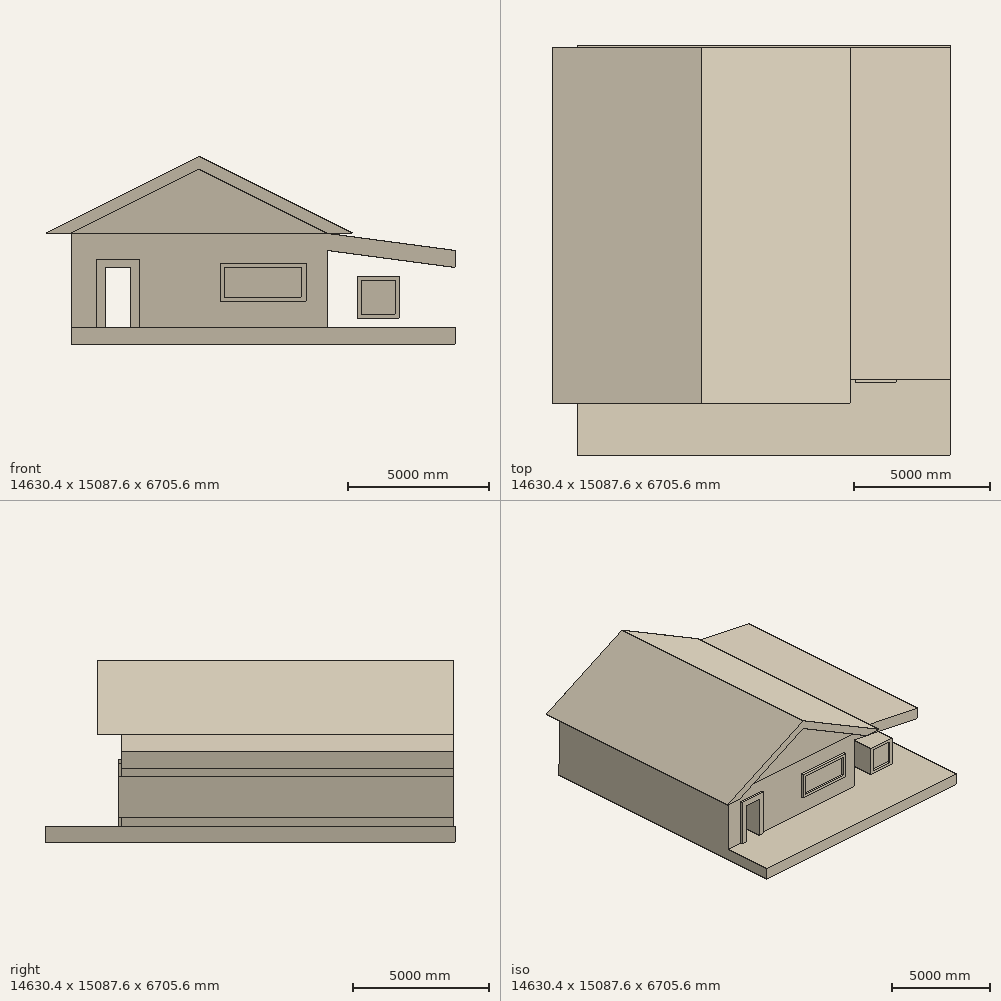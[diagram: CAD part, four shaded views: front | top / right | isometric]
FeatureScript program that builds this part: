
annotation { "Feature Type Name" : "Feature", "Feature Type Description" : "" }
export const myFeature = defineFeature(function(context is Context, id is Id, definition is map)
    precondition{}
    {
        {
            var Q0;
            Q0=qCreatedBy(makeId("Front.planeOp"),FACE);
            var sketch = newSketch(context, id + "F0", { "sketchPlane" : qUnion([Q0])});
            skLineSegment(sketch, "E0.bottom", {"start": v(-4572, 1676.4) * mm, "end": v(4572, 1676.4) * mm});
            skLineSegment(sketch, "E0.top", {"start": v(-4572, -1676.4) * mm, "end": v(4572, -1676.4) * mm});
            skLineSegment(sketch, "E0.left", {"start": v(-4572, 1676.4) * mm, "end": v(-4572, -1676.4) * mm});
            skLineSegment(sketch, "E0.right", {"start": v(4572, 1676.4) * mm, "end": v(4572, -1676.4) * mm});
            skPoint(sketch, "E0.middle", {"position": v(0, 0) * mm});
            skLineSegment(sketch, "E1", {"start": v(0, 1676.4) * mm, "end": v(0, 3962.4) * mm});
            skPoint(sketch, "E1.endSnap0", {"position": v(0, 1676.4) * mm});
            skLineSegment(sketch, "E2", {"start": v(0, 3962.4) * mm, "end": v(-4572, 1676.4) * mm});
            skLineSegment(sketch, "E3", {"start": v(0, 3962.4) * mm, "end": v(4572, 1676.4) * mm});
            skLineSegment(sketch, "E4", {"start": v(0, 3962.4) * mm, "end": v(0, 4419.6) * mm});
            skLineSegment(sketch, "E5", {"start": v(-4572, 1676.4) * mm, "end": v(-5486.4, 1676.4) * mm});
            skLineSegment(sketch, "E6", {"start": v(4572, 1676.4) * mm, "end": v(5486.4, 1676.4) * mm});
            skLineSegment(sketch, "E7", {"start": v(-5486.4, 1676.4) * mm, "end": v(0, 4419.6) * mm});
            skLineSegment(sketch, "E8", {"start": v(5486.4, 1676.4) * mm, "end": v(0, 4419.6) * mm});
            skLineSegment(sketch, "E9", {"start": v(-4572, -1676.4) * mm, "end": v(-4572, -2286) * mm});
            skLineSegment(sketch, "E10", {"start": v(4572, -1676.4) * mm, "end": v(4572, -2286) * mm});
            skLineSegment(sketch, "E11", {"start": v(4572, -2286) * mm, "end": v(-4572, -2286) * mm});
            skLineSegment(sketch, "E12", {"start": v(4572, -2286) * mm, "end": v(9144, -2286) * mm});
            skLineSegment(sketch, "E13", {"start": v(9144, -2286) * mm, "end": v(9144, -1676.4) * mm});
            skLineSegment(sketch, "E14", {"start": v(9144, -1676.4) * mm, "end": v(4572, -1676.4) * mm});
            skLineSegment(sketch, "E15", {"start": v(9144, -1676.4) * mm, "end": v(9144, 1066.8) * mm});
            skLineSegment(sketch, "E16", {"start": v(9144, 1066.8) * mm, "end": v(9144, 457.2) * mm});
            skLineSegment(sketch, "E17", {"start": v(4572, 1676.4) * mm, "end": v(4572, 1066.8) * mm});
            skLineSegment(sketch, "E18", {"start": v(9144, 457.2) * mm, "end": v(4572, 1066.8) * mm});
            skLineSegment(sketch, "E19", {"start": v(9144, 1066.8) * mm, "end": v(4572, 1676.4) * mm});
            skLineSegment(sketch, "E20.bottom", {"start": v(914.4, 457.2) * mm, "end": v(3657.6, 457.2) * mm});
            skLineSegment(sketch, "E20.top", {"start": v(914.4, -609.6) * mm, "end": v(3657.6, -609.6) * mm});
            skLineSegment(sketch, "E20.left", {"start": v(914.4, 457.2) * mm, "end": v(914.4, -609.6) * mm});
            skLineSegment(sketch, "E20.right", {"start": v(3657.6, 457.2) * mm, "end": v(3657.6, -609.6) * mm});
            skLineSegment(sketch, "E21.0", {"start": v(762, 609.6) * mm, "end": v(3810, 609.6) * mm});
            skLineSegment(sketch, "E21.1", {"start": v(762, 609.6) * mm, "end": v(762, -762) * mm});
            skLineSegment(sketch, "E21.2", {"start": v(762, -762) * mm, "end": v(3810, -762) * mm});
            skLineSegment(sketch, "E21.3", {"start": v(3810, 609.6) * mm, "end": v(3810, -762) * mm});
            skLineSegment(sketch, "E22.bottom", {"start": v(5791.2, 0) * mm, "end": v(7010.4, 0) * mm});
            skLineSegment(sketch, "E22.top", {"start": v(5791.2, -1219.2) * mm, "end": v(7010.4, -1219.2) * mm});
            skLineSegment(sketch, "E22.left", {"start": v(5791.2, 0) * mm, "end": v(5791.2, -1219.2) * mm});
            skLineSegment(sketch, "E22.right", {"start": v(7010.4, 0) * mm, "end": v(7010.4, -1219.2) * mm});
            skLineSegment(sketch, "E23.0", {"start": v(5638.8, 152.4) * mm, "end": v(7162.8, 152.4) * mm});
            skLineSegment(sketch, "E23.1", {"start": v(5638.8, 152.4) * mm, "end": v(5638.8, -1371.6) * mm});
            skLineSegment(sketch, "E23.2", {"start": v(5638.8, -1371.6) * mm, "end": v(7162.8, -1371.6) * mm});
            skLineSegment(sketch, "E23.3", {"start": v(7162.8, 152.4) * mm, "end": v(7162.8, -1371.6) * mm});
            skLineSegment(sketch, "E24.bottom", {"start": v(-3352.8, -1676.4) * mm, "end": v(-2438.4, -1676.4) * mm});
            skLineSegment(sketch, "E24.top", {"start": v(-3352.8, 457.2) * mm, "end": v(-2438.4, 457.2) * mm});
            skLineSegment(sketch, "E24.left", {"start": v(-3352.8, -1676.4) * mm, "end": v(-3352.8, 457.2) * mm});
            skLineSegment(sketch, "E24.right", {"start": v(-2438.4, -1676.4) * mm, "end": v(-2438.4, 457.2) * mm});
            skLineSegment(sketch, "E25.0", {"start": v(-2133.6, -1676.4) * mm, "end": v(-2133.6, 762) * mm});
            skLineSegment(sketch, "E25.1", {"start": v(-3657.6, 762) * mm, "end": v(-2133.6, 762) * mm});
            skLineSegment(sketch, "E25.2", {"start": v(-3657.6, -1676.4) * mm, "end": v(-3657.6, 762) * mm});
            skSolve(sketch);
        }
        {
            var Q0;
            Q0=makeQuery(id+"F0.imprint","IMPRINT",FACE,{"disambiguationData":[TD([[makeQuery(id+"F0.imprint","IMPRINT",EDGE,{"derivedFrom":sQuery(id+"F0.wireOp",EDGE,"E2")}),-1.0]])]});
            var Q1;
            Q1=makeQuery(id+"F0.imprint","IMPRINT",FACE,{"disambiguationData":[TD([[makeQuery(id+"F0.imprint","IMPRINT",EDGE,{"derivedFrom":sQuery(id+"F0.wireOp",EDGE,"E3")}),1.0]])]});
            var Q2;
            Q2=makeQuery(id+"F0.imprint","IMPRINT",FACE,{"disambiguationData":[TD([[makeQuery(id+"F0.imprint","IMPRINT",EDGE,{"derivedFrom":sQuery(id+"F0.wireOp",EDGE,"E16")}),-1.0]])]});
            extrude(context, id + "F1", {"entities" : qUnion([Q0, Q1, Q2]), "depth" : 914.4 * mm, "offsetDistance" : 30.48 * mm, "hasSecondDirection" : true, "secondDirectionOppositeDirection" : true, "secondDirectionDepth" : 12192 * mm});
        }
        {
            var Q0;
            {var subQ2=sQuery(id+"F0.wireOp",EDGE,"E1");Q0=makeQuery(id+"F0.imprint","IMPRINT",FACE,{"disambiguationData":[TD([[makeQuery(id+"F0.imprint","IMPRINT",EDGE,{"derivedFrom":subQ2}),1.0]])]});}
            var Q1;
            {var subQ2=sQuery(id+"F0.wireOp",EDGE,"E1");Q1=makeQuery(id+"F0.imprint","IMPRINT",FACE,{"disambiguationData":[TD([[makeQuery(id+"F0.imprint","IMPRINT",EDGE,{"derivedFrom":subQ2}),-1.0]])]});}
            extrude(context, id + "F2", {"entities" : qUnion([Q0, Q1]), "operationType" : NewBodyOperationType.ADD, "depth" : 304.8 * mm, "offsetDistance" : 30.48 * mm, "hasSecondDirection" : true, "secondDirectionOppositeDirection" : true, "secondDirectionDepth" : 12192 * mm});
        }
        {
            var Q0;
            {var subQ1=sQuery(id+"F0.wireOp",EDGE,"E0.left");Q0=makeQuery(id+"F0.imprint","IMPRINT",FACE,{"disambiguationData":[TD([[makeQuery(id+"F0.imprint","IMPRINT",EDGE,{"derivedFrom":subQ1}),1.0]])]});}
            var Q1;
            Q1=makeQuery(id+"F0.imprint","IMPRINT",FACE,{"disambiguationData":[TD([[makeQuery(id+"F0.imprint","IMPRINT",EDGE,{"derivedFrom":sQuery(id+"F0.wireOp",EDGE,"E24.bottom")}),1.0]])]});
            var Q2;
            Q2=makeQuery(id+"F0.imprint","IMPRINT",FACE,{"disambiguationData":[TD([[makeQuery(id+"F0.imprint","IMPRINT",EDGE,{"derivedFrom":sQuery(id+"F0.wireOp",EDGE,"E24.top")}),1.0]])]});
            var Q3;
            Q3=makeQuery(id+"F0.imprint","IMPRINT",FACE,{"disambiguationData":[TD([[makeQuery(id+"F0.imprint","IMPRINT",EDGE,{"derivedFrom":sQuery(id+"F0.wireOp",EDGE,"E20.bottom")}),-1.0]])]});
            var Q4;
            Q4=makeQuery(id+"F0.imprint","IMPRINT",FACE,{"disambiguationData":[TD([[makeQuery(id+"F0.imprint","IMPRINT",EDGE,{"derivedFrom":sQuery(id+"F0.wireOp",EDGE,"E20.bottom")}),1.0]])]});
            var Q5;
            Q5=makeQuery(id+"F0.imprint","IMPRINT",FACE,{"disambiguationData":[TD([[makeQuery(id+"F0.imprint","IMPRINT",EDGE,{"derivedFrom":sQuery(id+"F0.wireOp",EDGE,"E0.right")}),1.0]])]});
            var Q6;
            Q6=makeQuery(id+"F0.imprint","IMPRINT",FACE,{"disambiguationData":[TD([[makeQuery(id+"F0.imprint","IMPRINT",EDGE,{"derivedFrom":sQuery(id+"F0.wireOp",EDGE,"E22.bottom")}),-1.0]])]});
            var Q7;
            Q7=makeQuery(id+"F0.imprint","IMPRINT",FACE,{"disambiguationData":[TD([[makeQuery(id+"F0.imprint","IMPRINT",EDGE,{"derivedFrom":sQuery(id+"F0.wireOp",EDGE,"E22.bottom")}),1.0]])]});
            extrude(context, id + "F3", {"entities" : qUnion([Q0, Q1, Q2, Q3, Q4, Q5, Q6, Q7]), "depth" : 30.48 * mm, "offsetDistance" : 30.48 * mm, "hasSecondDirection" : true, "secondDirectionOppositeDirection" : true, "secondDirectionDepth" : 12192 * mm});
        }
        {
            var Q0;
            Q0=makeQuery(id+"F0.imprint","IMPRINT",FACE,{"disambiguationData":[TD([[makeQuery(id+"F0.imprint","IMPRINT",EDGE,{"derivedFrom":sQuery(id+"F0.wireOp",EDGE,"E24.top")}),1.0]])]});
            var Q1;
            Q1=makeQuery(id+"F0.imprint","IMPRINT",FACE,{"disambiguationData":[TD([[makeQuery(id+"F0.imprint","IMPRINT",EDGE,{"derivedFrom":sQuery(id+"F0.wireOp",EDGE,"E20.bottom")}),1.0]])]});
            var Q2;
            Q2=makeQuery(id+"F0.imprint","IMPRINT",FACE,{"disambiguationData":[TD([[makeQuery(id+"F0.imprint","IMPRINT",EDGE,{"derivedFrom":sQuery(id+"F0.wireOp",EDGE,"E22.bottom")}),1.0]])]});
            extrude(context, id + "F4", {"entities" : qUnion([Q0, Q1, Q2]), "operationType" : NewBodyOperationType.ADD, "depth" : 152.4 * mm, "offsetDistance" : 30.48 * mm});
        }
        {
            var Q0;
            Q0=makeQuery(id+"F0.imprint","IMPRINT",FACE,{"disambiguationData":[TD([[makeQuery(id+"F0.imprint","IMPRINT",EDGE,{"derivedFrom":sQuery(id+"F0.wireOp",EDGE,"E10")}),1.0]])]});
            var Q1;
            {var subQ3=sQuery(id+"F0.wireOp",EDGE,"E9");Q1=makeQuery(id+"F0.imprint","IMPRINT",FACE,{"disambiguationData":[TD([[makeQuery(id+"F0.imprint","IMPRINT",EDGE,{"derivedFrom":subQ3}),1.0]])]});}
            extrude(context, id + "F5", {"entities" : qUnion([Q0, Q1]), "operationType" : NewBodyOperationType.ADD, "depth" : 2834.64 * mm, "offsetDistance" : 30.48 * mm, "hasSecondDirection" : true, "secondDirectionOppositeDirection" : true, "secondDirectionDepth" : 12252.96 * mm});
        }
        {
            var Q0;
            Q0=makeQuery(id+"F5.boolean.opBoolean","MERGE",FACE,{"derivedFrom":[makeQuery(id+"F3.opExtrude","SWEPT_FACE",FACE,{"disambiguationData":[OSD([sQuery(id+"F0.wireOp",EDGE,"E0.left")])]}),makeQuery(id+"F5.opExtrude","SWEPT_FACE",FACE,{"disambiguationData":[OSD([sQuery(id+"F0.wireOp",EDGE,"E9")])]})]});
            var sketch = newSketch(context, id + "F6", { "sketchPlane" : qUnion([Q0])});
            skLineSegment(sketch, "E26.bottom", {"start": v(-9448.8, 762) * mm, "end": v(-2438.4, 762) * mm});
            skLineSegment(sketch, "E26.top", {"start": v(-9448.8, -1371.6) * mm, "end": v(-2438.4, -1371.6) * mm});
            skLineSegment(sketch, "E26.left", {"start": v(-9448.8, 762) * mm, "end": v(-9448.8, -1371.6) * mm});
            skLineSegment(sketch, "E26.right", {"start": v(-2438.4, 762) * mm, "end": v(-2438.4, -1371.6) * mm});
            skLineSegment(sketch, "E27.0", {"start": v(-9753.6, 1066.8) * mm, "end": v(-2133.6, 1066.8) * mm});
            skLineSegment(sketch, "E27.1", {"start": v(-9753.6, 1066.8) * mm, "end": v(-9753.6, -1676.4) * mm});
            skLineSegment(sketch, "E27.2", {"start": v(-9753.6, -1676.4) * mm, "end": v(-2133.6, -1676.4) * mm});
            skLineSegment(sketch, "E27.3", {"start": v(-2133.6, 1066.8) * mm, "end": v(-2133.6, -1676.4) * mm});
            skSolve(sketch);
        }
        {
            var Q0;
            Q0=sQuery(id+"F6.wireOp",EDGE,"E26.bottom");
            var Q1;
            Q1=sQuery(id+"F6.wireOp",EDGE,"E26.left");
            var Q2;
            Q2=sQuery(id+"F6.wireOp",EDGE,"E26.right");
            var Q3;
            Q3=sQuery(id+"F6.wireOp",EDGE,"E26.top");
            extrude(context, id + "F7", {"bodyType" : ToolBodyType.SURFACE, "surfaceEntities" : qUnion([Q0, Q1, Q2, Q3]), "depth" : 91.44 * mm, "offsetDistance" : 30.48 * mm});
        }
        {
            var Q0;
            Q0=sQuery(id+"F6.wireOp",EDGE,"E27.0");
            var Q1;
            Q1=sQuery(id+"F6.wireOp",EDGE,"E27.1");
            var Q2;
            Q2=sQuery(id+"F6.wireOp",EDGE,"E27.2");
            var Q3;
            Q3=sQuery(id+"F6.wireOp",EDGE,"E27.3");
            extrude(context, id + "F8", {"bodyType" : ToolBodyType.SURFACE, "surfaceEntities" : qUnion([Q0, Q1, Q2, Q3]), "depth" : 152.4 * mm, "offsetDistance" : 30.48 * mm});
        }
    });
